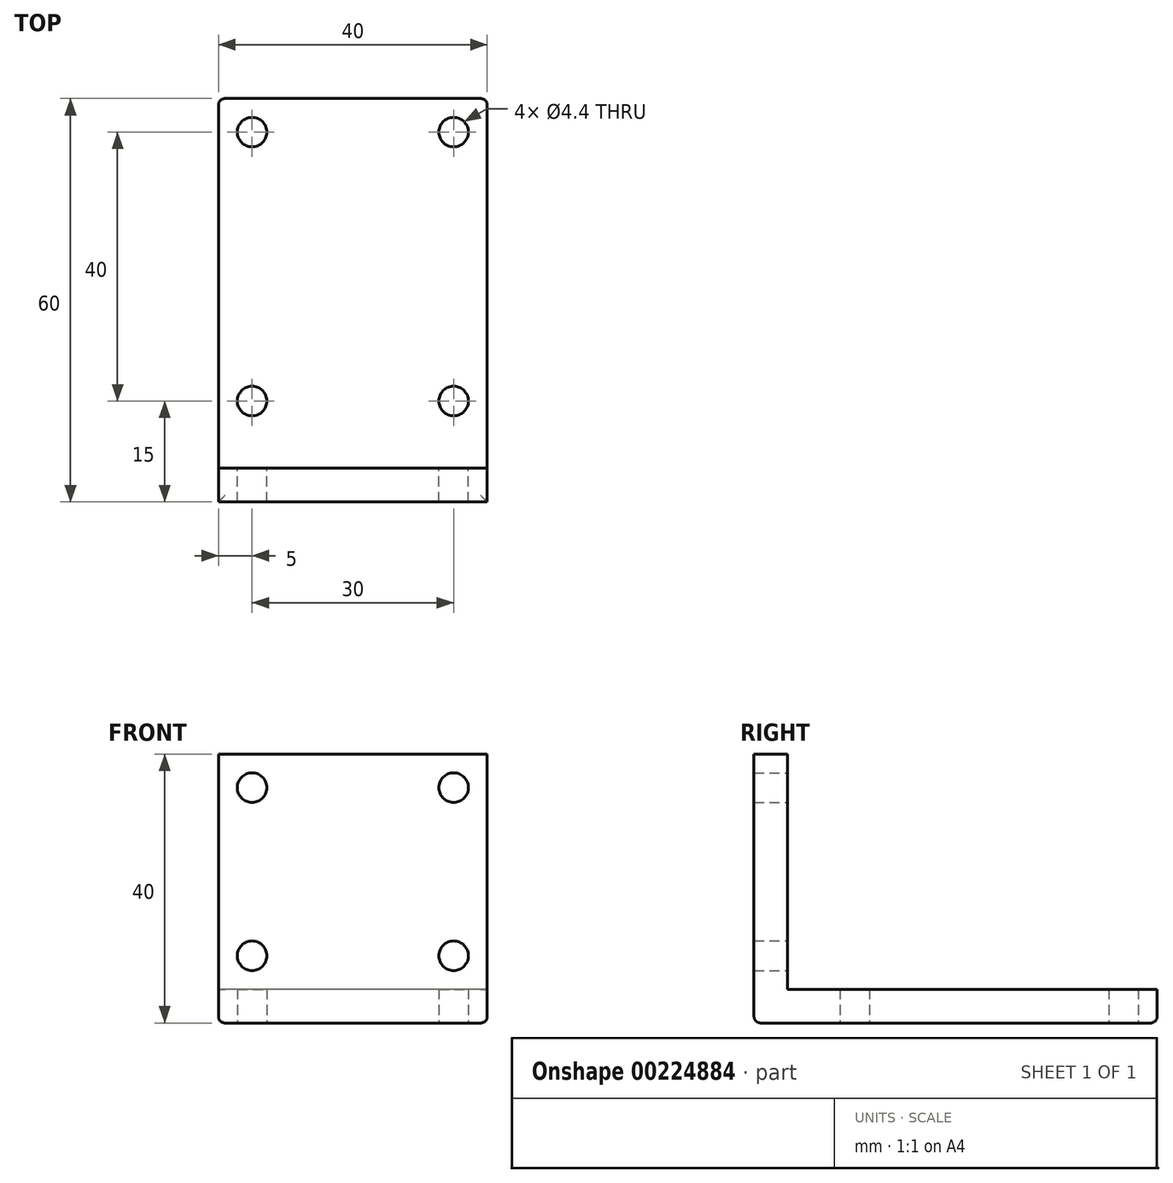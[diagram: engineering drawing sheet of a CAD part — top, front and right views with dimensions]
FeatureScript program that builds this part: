
annotation { "Feature Type Name" : "Feature", "Feature Type Description" : "" }
export const myFeature = defineFeature(function(context is Context, id is Id, definition is map)
    precondition{}
    {
        {
            var Q0;
            Q0=qCreatedBy(makeId("Right.planeOp"),FACE);
            var sketch = newSketch(context, id + "F0", { "sketchPlane" : qUnion([Q0])});
            skLineSegment(sketch, "E0", {"start": v(0, 40) * mm, "end": v(0, 0) * mm});
            skLineSegment(sketch, "E1", {"start": v(0, 0) * mm, "end": v(60, 0) * mm});
            skLineSegment(sketch, "E2", {"start": v(60, 0) * mm, "end": v(60, 5) * mm});
            skLineSegment(sketch, "E3", {"start": v(60, 5) * mm, "end": v(5, 5) * mm});
            skLineSegment(sketch, "E4", {"start": v(5, 5) * mm, "end": v(5, 40) * mm});
            skLineSegment(sketch, "E5", {"start": v(5, 40) * mm, "end": v(0, 40) * mm});
            skSolve(sketch);
        }
        {
            var Q0;
            Q0=makeQuery(id+"F0.imprint","IMPRINT",FACE,{"disambiguationData":[TD([[makeQuery(id+"F0.imprint","IMPRINT",EDGE,{"derivedFrom":sQuery(id+"F0.wireOp",EDGE,"E0")}),1.0]])]});
            extrude(context, id + "F1", {"entities" : qUnion([Q0]), "depth" : 40 * mm});
        }
        {
            var Q0;
            Q0=makeQuery(id+"F1.opExtrude","SWEPT_FACE",FACE,{"disambiguationData":[OSD([sQuery(id+"F0.wireOp",EDGE,"E4")])]});
            var sketch = newSketch(context, id + "F2", { "sketchPlane" : qUnion([Q0])});
            skPoint(sketch, "E6", {"position": v(-35, 35) * mm});
            skPoint(sketch, "E7", {"position": v(-5, 35) * mm});
            skPoint(sketch, "E8", {"position": v(-5, 10) * mm});
            skPoint(sketch, "E9", {"position": v(-35, 10) * mm});
            skSolve(sketch);
        }
        {
            var Q0;
            Q0=sQuery(id+"F2.wireOp",VERTEX,"E6");
            var Q1;
            Q1=sQuery(id+"F2.wireOp",VERTEX,"E7");
            var Q2;
            Q2=sQuery(id+"F2.wireOp",VERTEX,"E8");
            var Q3;
            Q3=sQuery(id+"F2.wireOp",VERTEX,"E9");
            var Q4;
            Q4=makeQuery(id+"F1.opExtrude","SWEPT_BODY",BODY,{"disambiguationData":[OSD([sQuery(id+"F0.wireOp",EDGE,"E0"),sQuery(id+"F0.wireOp",EDGE,"E1"),sQuery(id+"F0.wireOp",EDGE,"E2"),sQuery(id+"F0.wireOp",EDGE,"E3"),sQuery(id+"F0.wireOp",EDGE,"E4"),sQuery(id+"F0.wireOp",EDGE,"E5")])]});
            hole(context, id + "F3", {"style" : HoleStyle.SIMPLE, "endStyle" : HoleEndStyle.THROUGH, "standardTappedOrClearance" : lookupTablePath({ "standard" : "ISO", "fit" : "Normal", "size" : "M4", "type" : "Clearance" }), "standardBlindInLast" : lookupTablePath({ "fit" : "Standard", "standard" : "ISO", "size" : "M4", "type" : "Clearance" }), "holeDiameter" : 4.4 * mm, "startFromSketch" : true, "locations" : qUnion([Q0, Q1, Q2, Q3]), "scope" : qUnion([Q4]), "isTappedThrough" : true});
        }
        {
            var Q0;
            Q0=makeQuery(id+"F1.opExtrude","SWEPT_FACE",FACE,{"disambiguationData":[OSD([sQuery(id+"F0.wireOp",EDGE,"E1")])]});
            var sketch = newSketch(context, id + "F4", { "sketchPlane" : qUnion([Q0])});
            skPoint(sketch, "E10", {"position": v(35, -55) * mm});
            skPoint(sketch, "E11", {"position": v(5, -55) * mm});
            skPoint(sketch, "E12", {"position": v(5, -15) * mm});
            skPoint(sketch, "E13", {"position": v(35, -15) * mm});
            skSolve(sketch);
        }
        {
            var Q0;
            Q0=sQuery(id+"F4.wireOp",VERTEX,"E10");
            var Q1;
            Q1=sQuery(id+"F4.wireOp",VERTEX,"E11");
            var Q2;
            Q2=sQuery(id+"F4.wireOp",VERTEX,"E12");
            var Q3;
            Q3=sQuery(id+"F4.wireOp",VERTEX,"E13");
            var Q4;
            Q4=makeQuery(id+"F1.opExtrude","SWEPT_BODY",BODY,{"disambiguationData":[OSD([sQuery(id+"F0.wireOp",EDGE,"E0"),sQuery(id+"F0.wireOp",EDGE,"E1"),sQuery(id+"F0.wireOp",EDGE,"E2"),sQuery(id+"F0.wireOp",EDGE,"E3"),sQuery(id+"F0.wireOp",EDGE,"E4"),sQuery(id+"F0.wireOp",EDGE,"E5")])]});
            hole(context, id + "F5", {"style" : HoleStyle.SIMPLE, "endStyle" : HoleEndStyle.THROUGH, "standardTappedOrClearance" : lookupTablePath({ "standard" : "ISO", "fit" : "Normal", "size" : "M4", "type" : "Clearance" }), "standardBlindInLast" : lookupTablePath({ "fit" : "Standard", "standard" : "ISO", "size" : "M4", "type" : "Clearance" }), "holeDiameter" : 4.4 * mm, "startFromSketch" : true, "locations" : qUnion([Q0, Q1, Q2, Q3]), "scope" : qUnion([Q4]), "isTappedThrough" : true});
        }
        {
            var Q0;
            Q0=makeQuery(id+"F1.opExtrude","CAP_EDGE",EDGE,{"disambiguationData":[OSD([sQuery(id+"F0.wireOp",EDGE,"E2")])],"isStart":false});
            var Q1;
            Q1=makeQuery(id+"F1.opExtrude","CAP_EDGE",EDGE,{"disambiguationData":[OSD([sQuery(id+"F0.wireOp",EDGE,"E2")])],"isStart":true});
            var Q2;
            Q2=makeQuery(id+"F1.opExtrude","SWEPT_EDGE",EDGE,{"disambiguationData":[OSD([sQuery(id+"F0.wireOp",EDGE,"E1"),sQuery(id+"F0.wireOp",EDGE,"E2")])]});
            var Q3;
            Q3=makeQuery(id+"F1.opExtrude","CAP_EDGE",EDGE,{"disambiguationData":[OSD([sQuery(id+"F0.wireOp",EDGE,"E1")])],"isStart":true});
            var Q4;
            Q4=makeQuery(id+"F1.opExtrude","SWEPT_EDGE",EDGE,{"disambiguationData":[OSD([sQuery(id+"F0.wireOp",EDGE,"E0"),sQuery(id+"F0.wireOp",EDGE,"E1")])]});
            var Q5;
            Q5=makeQuery(id+"F1.opExtrude","CAP_EDGE",EDGE,{"disambiguationData":[OSD([sQuery(id+"F0.wireOp",EDGE,"E1")])],"isStart":false});
            fillet(context, id + "F6", {"entities" : qUnion([Q0, Q1, Q2, Q3, Q4, Q5]), "radius" : 1 * mm, "tangentPropagation" : true, "allowEdgeOverflow" : false});
        }
    });
